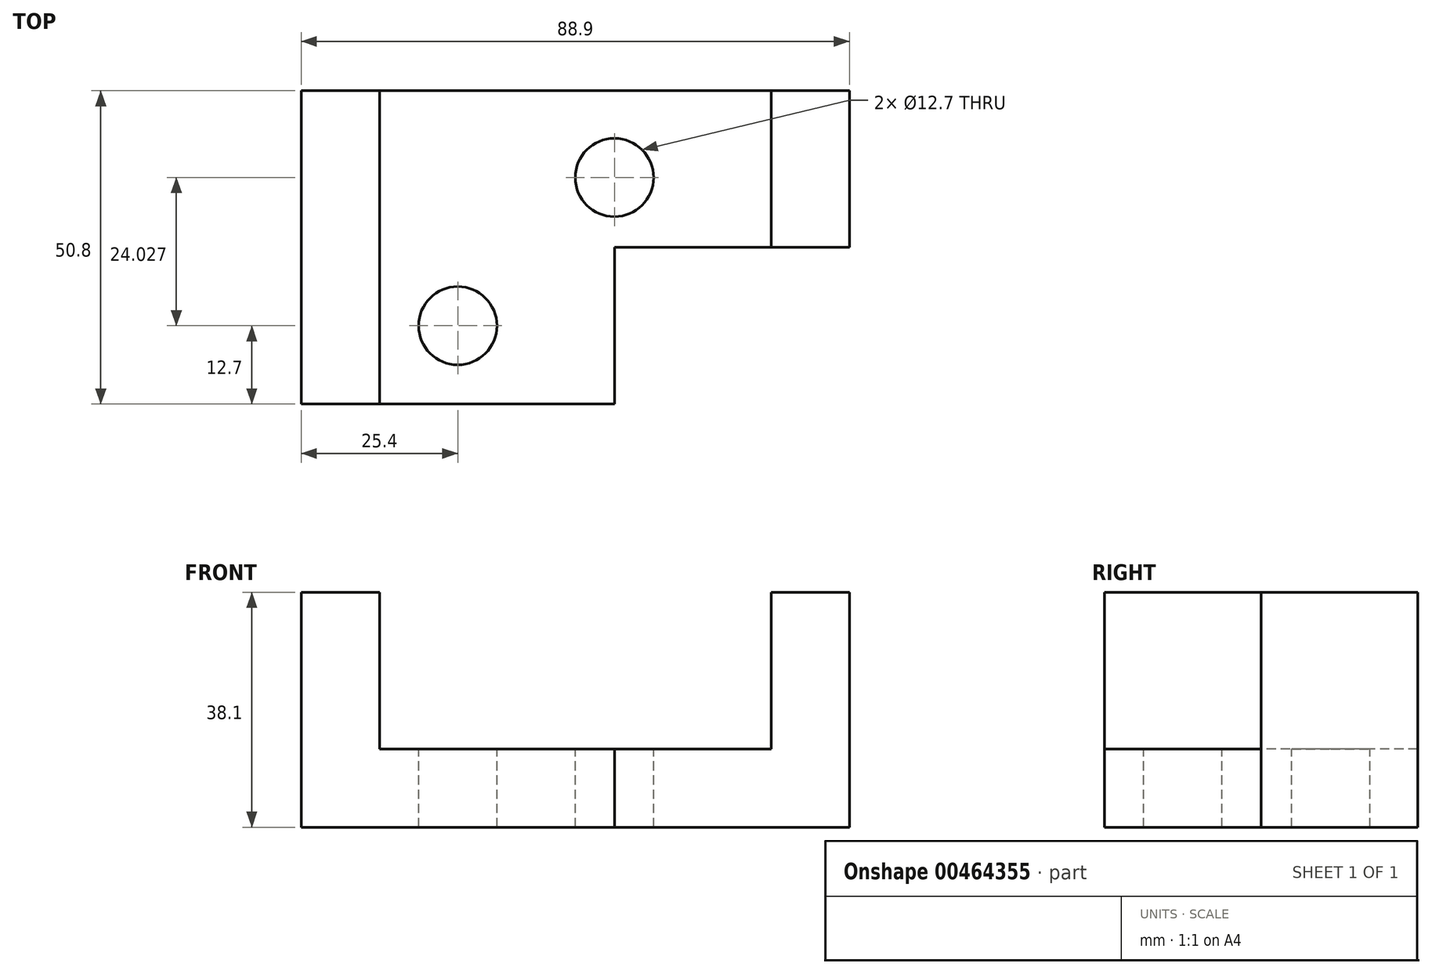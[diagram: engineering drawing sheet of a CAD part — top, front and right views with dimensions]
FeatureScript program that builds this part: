
annotation { "Feature Type Name" : "Feature", "Feature Type Description" : "" }
export const myFeature = defineFeature(function(context is Context, id is Id, definition is map)
    precondition{}
    {
        {
            var Q0;
            Q0=qCreatedBy(makeId("Front.planeOp"),FACE);
            var sketch = newSketch(context, id + "F0", { "sketchPlane" : qUnion([Q0])});
            skLineSegment(sketch, "E0.bottom", {"start": v(-44.45, 19.05) * mm, "end": v(44.45, 19.05) * mm});
            skLineSegment(sketch, "E0.top", {"start": v(-44.45, -19.05) * mm, "end": v(44.45, -19.05) * mm});
            skLineSegment(sketch, "E0.left", {"start": v(-44.45, 19.05) * mm, "end": v(-44.45, -19.05) * mm});
            skLineSegment(sketch, "E0.right", {"start": v(44.45, 19.05) * mm, "end": v(44.45, -19.05) * mm});
            skPoint(sketch, "E0.middle", {"position": v(0, 0) * mm});
            skSolve(sketch);
        }
        {
            var Q0;
            Q0 = qSketchRegion(id + "F0", true);
            extrude(context, id + "F1", {"entities" : qUnion([Q0]), "depth" : 50.8 * mm});
        }
        {
            var Q0;
            Q0=makeQuery(id+"F1.opExtrude","CAP_FACE",FACE,{"disambiguationData":[OSD([sQuery(id+"F0.wireOp",EDGE,"E0.bottom"),sQuery(id+"F0.wireOp",EDGE,"E0.top"),sQuery(id+"F0.wireOp",EDGE,"E0.left"),sQuery(id+"F0.wireOp",EDGE,"E0.right")])],"isStart":false});
            var sketch = newSketch(context, id + "F2", { "sketchPlane" : qUnion([Q0])});
            skLineSegment(sketch, "E1.bottom", {"start": v(-31.75, 19.05) * mm, "end": v(31.75, 19.05) * mm});
            skLineSegment(sketch, "E1.top", {"start": v(-31.75, -6.35) * mm, "end": v(31.75, -6.35) * mm});
            skLineSegment(sketch, "E1.left", {"start": v(-31.75, 19.05) * mm, "end": v(-31.75, -6.35) * mm});
            skLineSegment(sketch, "E1.right", {"start": v(31.75, 19.05) * mm, "end": v(31.75, -6.35) * mm});
            skSolve(sketch);
        }
        {
            var Q0;
            Q0 = qSketchRegion(id + "F2", true);
            extrude(context, id + "F3", {"entities" : qUnion([Q0]), "operationType" : NewBodyOperationType.REMOVE, "endBound" : BoundingType.THROUGH_ALL, "oppositeDirection" : true, "depth" : 25.4 * mm});
        }
        {
            var Q0;
            {var subQ0=sQuery(id+"F0.wireOp",EDGE,"E0.right");var subQ3=sQuery(id+"F0.wireOp",EDGE,"E0.bottom");Q0=makeQuery(id+"F3.boolean.opBoolean","SPLIT",FACE,{"disambiguationData":[TD([makeQuery(id+"F1.opExtrude","SWEPT_FACE",FACE,{"disambiguationData":[OSD([subQ0])]})])],"derivedFrom":makeQuery(id+"F1.opExtrude","SWEPT_FACE",FACE,{"disambiguationData":[OSD([subQ3])]})});}
            var sketch = newSketch(context, id + "F4", { "sketchPlane" : qUnion([Q0])});
            skLineSegment(sketch, "E2.bottom", {"start": v(44.45, -50.8) * mm, "end": v(6.35, -50.8) * mm});
            skLineSegment(sketch, "E2.top", {"start": v(44.45, -25.4) * mm, "end": v(6.35, -25.4) * mm});
            skLineSegment(sketch, "E2.left", {"start": v(44.45, -50.8) * mm, "end": v(44.45, -25.4) * mm});
            skLineSegment(sketch, "E2.right", {"start": v(6.35, -50.8) * mm, "end": v(6.35, -25.4) * mm});
            skSolve(sketch);
        }
        {
            var Q0;
            Q0 = qSketchRegion(id + "F4", true);
            extrude(context, id + "F5", {"entities" : qUnion([Q0]), "operationType" : NewBodyOperationType.REMOVE, "endBound" : BoundingType.THROUGH_ALL, "oppositeDirection" : true, "depth" : 25.4 * mm});
        }
        {
            var Q0;
            Q0=makeQuery(id+"F3.boolean.opBoolean","COPY",FACE,{"derivedFrom":makeQuery(id+"F3.opExtrude","SWEPT_FACE",FACE,{"disambiguationData":[OSD([sQuery(id+"F2.wireOp",EDGE,"E1.top")])]})});
            var sketch = newSketch(context, id + "F6", { "sketchPlane" : qUnion([Q0])});
            skCircle(sketch, "E3", {"center": v(-19.05, -38.1) * mm, "radius": 6.35 * mm});
            skSolve(sketch);
        }
        {
            var Q0;
            Q0 = qSketchRegion(id + "F6", true);
            extrude(context, id + "F7", {"entities" : qUnion([Q0]), "operationType" : NewBodyOperationType.REMOVE, "endBound" : BoundingType.THROUGH_ALL, "oppositeDirection" : true, "depth" : 25.4 * mm});
        }
        {
            var Q0;
            Q0=makeQuery(id+"F3.boolean.opBoolean","COPY",FACE,{"derivedFrom":makeQuery(id+"F3.opExtrude","SWEPT_FACE",FACE,{"disambiguationData":[OSD([sQuery(id+"F2.wireOp",EDGE,"E1.top")])]})});
            var sketch = newSketch(context, id + "F8", { "sketchPlane" : qUnion([Q0])});
            skCircle(sketch, "E4", {"center": v(6.35, -14.07) * mm, "radius": 6.35 * mm});
            skSolve(sketch);
        }
        {
            var Q0;
            Q0 = qSketchRegion(id + "F8", true);
            extrude(context, id + "F9", {"entities" : qUnion([Q0]), "operationType" : NewBodyOperationType.REMOVE, "endBound" : BoundingType.THROUGH_ALL, "oppositeDirection" : true, "depth" : 25.4 * mm});
        }
    });
